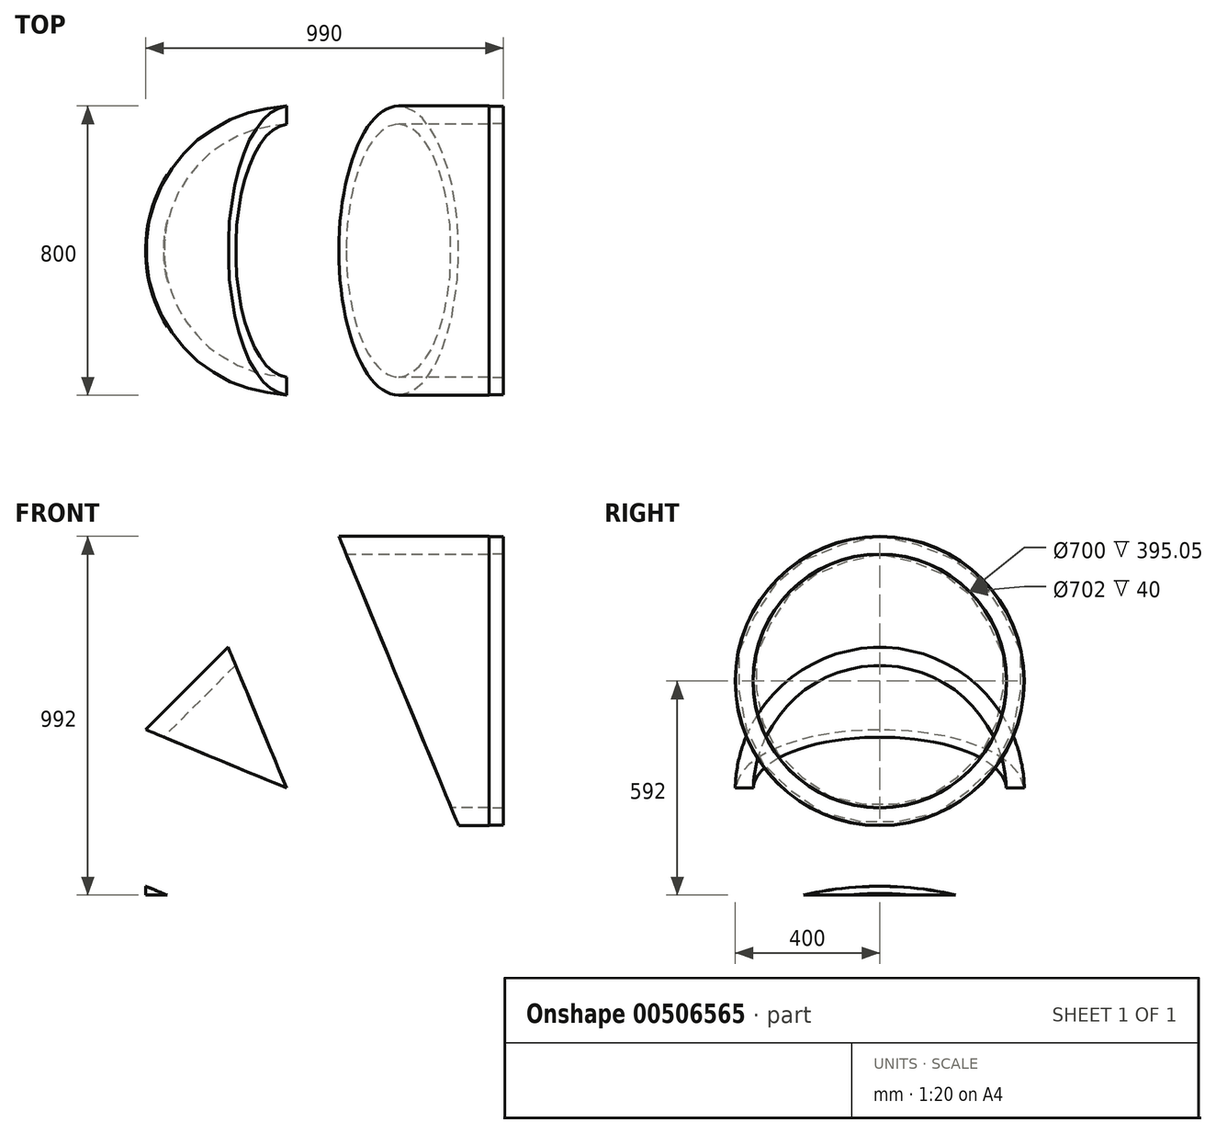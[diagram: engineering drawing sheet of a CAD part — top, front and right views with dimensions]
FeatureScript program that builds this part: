
annotation { "Feature Type Name" : "Feature", "Feature Type Description" : "" }
export const myFeature = defineFeature(function(context is Context, id is Id, definition is map)
    precondition{}
    {
        {
            var Q0;
            Q0=qCreatedBy(makeId("Front.planeOp"),FACE);
            var sketch = newSketch(context, id + "F0", { "sketchPlane" : qUnion([Q0])});
            skLineSegment(sketch, "E0", {"start": v(0, 0) * mm, "end": v(0, -525.84) * mm, "construction": true});
            skLineSegment(sketch, "E1", {"start": v(-400, -592) * mm, "end": v(-399, -592) * mm});
            skLineSegment(sketch, "E2", {"start": v(-399, -592) * mm, "end": v(-399, -552) * mm});
            skLineSegment(sketch, "E3", {"start": v(-399, -552) * mm, "end": v(-351, -552) * mm});
            skLineSegment(sketch, "E4", {"start": v(-351, -552) * mm, "end": v(-351, -592) * mm});
            skLineSegment(sketch, "E5", {"start": v(-351, -592) * mm, "end": v(-350, -592) * mm});
            skLineSegment(sketch, "E6", {"start": v(0, 0) * mm, "end": v(-755.87, 0) * mm, "construction": true});
            skLineSegment(sketch, "E7", {"start": v(-400, -592) * mm, "end": v(-400, -134.31) * mm});
            skLineSegment(sketch, "E8", {"start": v(-350, -592) * mm, "end": v(-350, -155.03) * mm});
            skLineSegment(sketch, "E9", {"start": v(0, 0) * mm, "end": v(738.22, 0) * mm, "construction": true});
            skLineSegment(sketch, "E10", {"start": v(550, 350) * mm, "end": v(550, 351) * mm});
            skLineSegment(sketch, "E11", {"start": v(550, 351) * mm, "end": v(590, 351) * mm});
            skLineSegment(sketch, "E12", {"start": v(590, 351) * mm, "end": v(590, 399) * mm});
            skLineSegment(sketch, "E13", {"start": v(590, 399) * mm, "end": v(550, 399) * mm});
            skLineSegment(sketch, "E14", {"start": v(550, 399) * mm, "end": v(550, 400) * mm});
            skLineSegment(sketch, "E15", {"start": v(550, 400) * mm, "end": v(134.31, 400) * mm});
            skLineSegment(sketch, "E16", {"start": v(-350, -155.03) * mm, "end": v(155.03, 350) * mm});
            skLineSegment(sketch, "E17", {"start": v(-350, -155.03) * mm, "end": v(-766.78, 17.61) * mm, "construction": true});
            skLineSegment(sketch, "E18", {"start": v(-350, -155.03) * mm, "end": v(-758.83, -155.03) * mm, "construction": true});
            skLineSegment(sketch, "E19", {"start": v(-350, -155.03) * mm, "end": v(-400, -134.31) * mm});
            skLineSegment(sketch, "E20", {"start": v(155.03, 350) * mm, "end": v(155.03, 793.16) * mm, "construction": true});
            skLineSegment(sketch, "E21", {"start": v(155.03, 350) * mm, "end": v(-11.64, 752.38) * mm, "construction": true});
            skLineSegment(sketch, "E22", {"start": v(155.03, 350) * mm, "end": v(134.31, 400) * mm});
            skLineSegment(sketch, "E23.trimOffspring", {"start": v(155.03, 350) * mm, "end": v(550, 350) * mm});
            skLineSegment(sketch, "E24", {"start": v(-400, -134.31) * mm, "end": v(134.31, 400) * mm});
            skLineSegment(sketch, "E25", {"start": v(-350, -155.03) * mm, "end": v(861.1, -656.68) * mm, "construction": true});
            skLineSegment(sketch, "E26", {"start": v(155.03, 350) * mm, "end": v(606.32, -739.53) * mm, "construction": true});
            skLineSegment(sketch, "E27", {"start": v(0, -300) * mm, "end": v(300, 0) * mm, "construction": true});
            skSolve(sketch);
        }
        {
            var Q0;
            Q0=qCreatedBy(makeId("Right.planeOp"),FACE);
            var sketch = newSketch(context, id + "F1", { "sketchPlane" : qUnion([Q0])});
            skLineSegment(sketch, "E28", {"start": v(288.35, -300) * mm, "end": v(-360.5, -300) * mm, "construction": true});
            skSolve(sketch);
        }
        {
            var Q0;
            Q0=sQuery(id+"F1.wireOp",EDGE,"E28");
            var Q1;
            Q1=sQuery(id+"F0.wireOp",EDGE,"E25");
            cPlane(context, id + "F2", {"entities" : qUnion([Q0, Q1]), "cplaneType" : CPlaneType.LINE_ANGLE, "offset" : 25 * mm, "angle" : 0 * degree, "width" : 150 * mm, "height" : 150 * mm});
        }
        {
            var Q0;
            Q0=qCreatedBy(makeId("Top.planeOp"),FACE);
            var sketch = newSketch(context, id + "F3", { "sketchPlane" : qUnion([Q0])});
            skLineSegment(sketch, "E29", {"start": v(300, 508.47) * mm, "end": v(300, -612.1) * mm, "construction": true});
            skSolve(sketch);
        }
        {
            var Q0;
            Q0=sQuery(id+"F3.wireOp",EDGE,"E29");
            var Q1;
            Q1=sQuery(id+"F0.wireOp",EDGE,"E26");
            cPlane(context, id + "F4", {"entities" : qUnion([Q0, Q1]), "cplaneType" : CPlaneType.LINE_ANGLE, "offset" : 25 * mm, "angle" : 0 * degree, "width" : 150 * mm, "height" : 150 * mm});
        }
        {
            var Q0;
            Q0=qCreatedBy(id+"F2.planeOp",FACE);
            var sketch = newSketch(context, id + "F5", { "sketchPlane" : qUnion([Q0])});
            skLineSegment(sketch, "E30.bottom", {"start": v(-815.8, -791.8) * mm, "end": v(1036.86, -791.8) * mm});
            skLineSegment(sketch, "E30.top", {"start": v(-815.8, 744.83) * mm, "end": v(1036.86, 744.83) * mm});
            skLineSegment(sketch, "E30.left", {"start": v(-815.8, -791.8) * mm, "end": v(-815.8, 744.83) * mm});
            skLineSegment(sketch, "E30.right", {"start": v(1036.86, -791.8) * mm, "end": v(1036.86, 744.83) * mm});
            skSolve(sketch);
        }
        {
            var Q0;
            Q0=qCreatedBy(id+"F4.planeOp",FACE);
            var sketch = newSketch(context, id + "F6", { "sketchPlane" : qUnion([Q0])});
            skLineSegment(sketch, "E31.bottom", {"start": v(754.29, -977.32) * mm, "end": v(-876.24, -977.32) * mm});
            skLineSegment(sketch, "E31.top", {"start": v(754.29, 712.75) * mm, "end": v(-876.24, 712.75) * mm});
            skLineSegment(sketch, "E31.left", {"start": v(754.29, -977.32) * mm, "end": v(754.29, 712.75) * mm});
            skLineSegment(sketch, "E31.right", {"start": v(-876.24, -977.32) * mm, "end": v(-876.24, 712.75) * mm});
            skSolve(sketch);
        }
        {
            var Q0;
            Q0=makeQuery(id+"F0.imprint","IMPRINT",FACE,{"disambiguationData":[TD([[makeQuery(id+"F0.imprint","IMPRINT",EDGE,{"derivedFrom":sQuery(id+"F0.wireOp",EDGE,"E1")}),1.0]])]});
            var Q1;
            Q1=sQuery(id+"F0.wireOp",EDGE,"E0");
            revolve(context, id + "F7", {"entities" : qUnion([Q0]), "axis" : qUnion([Q1]), "revolveType" : RevolveType.FULL});
        }
        {
            var Q0;
            Q0=makeQuery(id+"F5.imprint","IMPRINT",FACE,{"disambiguationData":[TD([[makeQuery(id+"F5.imprint","IMPRINT",EDGE,{"derivedFrom":sQuery(id+"F5.wireOp",EDGE,"E30.bottom")}),1.0]])]});
            var Q1;
            Q1=makeQuery(id+"F7.opRevolve","SWEPT_BODY",BODY,{"disambiguationData":[OSD([sQuery(id+"F0.wireOp",EDGE,"E1"),sQuery(id+"F0.wireOp",EDGE,"E2"),sQuery(id+"F0.wireOp",EDGE,"E3"),sQuery(id+"F0.wireOp",EDGE,"E4"),sQuery(id+"F0.wireOp",EDGE,"E5"),sQuery(id+"F0.wireOp",EDGE,"E7"),sQuery(id+"F0.wireOp",EDGE,"E8"),sQuery(id+"F0.wireOp",EDGE,"E19")])]});
            extrude(context, id + "F8", {"entities" : qUnion([Q0]), "operationType" : NewBodyOperationType.REMOVE, "endBoundEntityBody" : qUnion([Q1]), "depth" : 400 * mm});
        }
        {
            var Q0;
            Q0=makeQuery(id+"F0.imprint","IMPRINT",FACE,{"disambiguationData":[TD([[makeQuery(id+"F0.imprint","IMPRINT",EDGE,{"derivedFrom":sQuery(id+"F0.wireOp",EDGE,"E16")}),1.0]])]});
            var Q1;
            Q1=sQuery(id+"F0.wireOp",EDGE,"E27");
            revolve(context, id + "F9", {"entities" : qUnion([Q0]), "axis" : qUnion([Q1]), "revolveType" : RevolveType.FULL});
        }
        {
            var Q0;
            Q0=makeQuery(id+"F5.imprint","IMPRINT",FACE,{"disambiguationData":[TD([[makeQuery(id+"F5.imprint","IMPRINT",EDGE,{"derivedFrom":sQuery(id+"F5.wireOp",EDGE,"E30.bottom")}),1.0]])]});
            extrude(context, id + "F10", {"entities" : qUnion([Q0]), "operationType" : NewBodyOperationType.REMOVE, "oppositeDirection" : true, "depth" : 400 * mm});
        }
        {
            var Q0;
            Q0=makeQuery(id+"F6.imprint","IMPRINT",FACE,{"disambiguationData":[TD([[makeQuery(id+"F6.imprint","IMPRINT",EDGE,{"derivedFrom":sQuery(id+"F6.wireOp",EDGE,"E31.bottom")}),-1.0]])]});
            extrude(context, id + "F11", {"entities" : qUnion([Q0]), "operationType" : NewBodyOperationType.REMOVE, "depth" : 400 * mm});
        }
        {
            var Q0;
            Q0=makeQuery(id+"F0.imprint","IMPRINT",FACE,{"disambiguationData":[TD([[makeQuery(id+"F0.imprint","IMPRINT",EDGE,{"derivedFrom":sQuery(id+"F0.wireOp",EDGE,"E10")}),1.0]])]});
            var Q1;
            Q1=sQuery(id+"F0.wireOp",EDGE,"E9");
            revolve(context, id + "F12", {"entities" : qUnion([Q0]), "axis" : qUnion([Q1]), "revolveType" : RevolveType.FULL});
        }
        {
            var Q0;
            Q0=makeQuery(id+"F6.imprint","IMPRINT",FACE,{"disambiguationData":[TD([[makeQuery(id+"F6.imprint","IMPRINT",EDGE,{"derivedFrom":sQuery(id+"F6.wireOp",EDGE,"E31.bottom")}),-1.0]])]});
            extrude(context, id + "F13", {"entities" : qUnion([Q0]), "operationType" : NewBodyOperationType.REMOVE, "oppositeDirection" : true, "depth" : 400 * mm});
        }
    });
